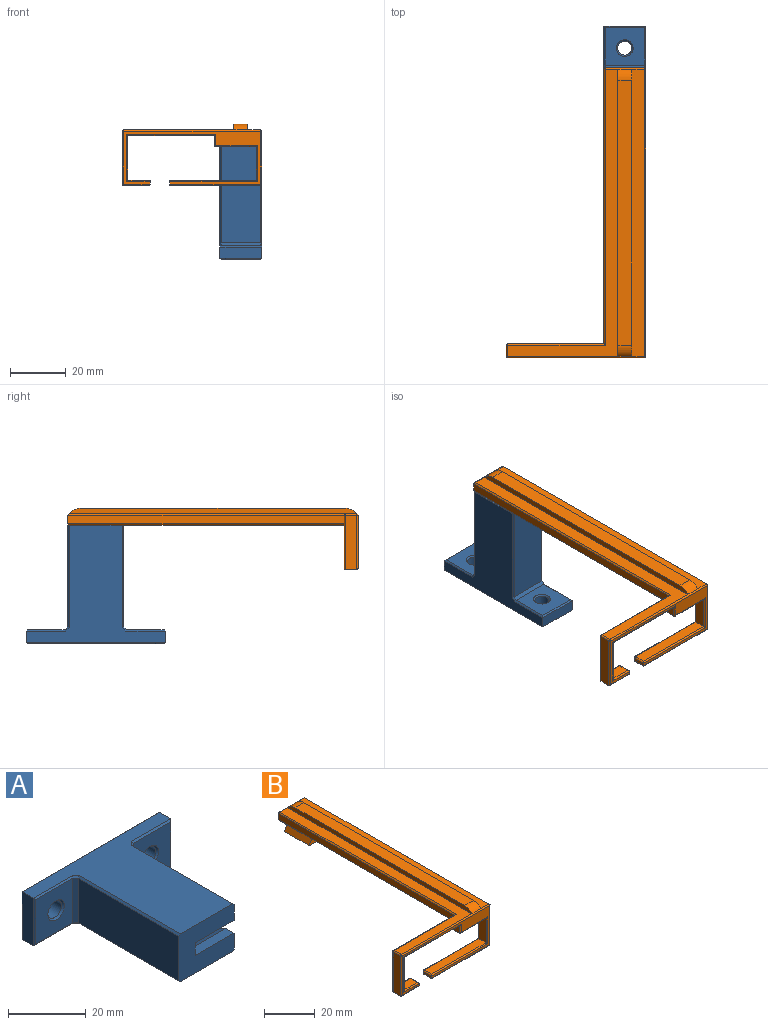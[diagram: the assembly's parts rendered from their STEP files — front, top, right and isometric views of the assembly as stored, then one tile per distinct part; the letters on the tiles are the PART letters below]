
ASSEMBLY  parts=2 mates=1
PART A: 42 faces, bbox 50x42.5x15 mm
  f0: plane 20x15mm, normal (0,-1,0), area 243.5mm2, adj f2,f4,f10,f11,f14,f18,f21,f26
  f1: plane 14x13.5mm, normal (0,-1,0), area 160.7mm2, adj f12,f23,f24,f25,f31
  f2: plane 50x42mm, normal (0,0,1), area 923.7mm2, adj f0,f3,f7,f14,f15,f16,f21,f22
  f3: plane 15x4mm, normal (-1,0,0), area 60mm2, adj f2,f4,f17,f35
  f4: plane 50x42mm, normal (0,0,-1), area 923.7mm2, adj f0,f3,f7,f18,f19,f20,f25,f26
  f5: cylinder r=2.5mm len=5mm, axis (0,1,0), area 62.8mm2, adj f29,f30
  f6: cylinder r=2.5mm len=5mm, axis (0,1,0), area 62.8mm2, adj f28,f31
  f7: plane 15x4mm, normal (1,0,0), area 60mm2, adj f2,f4,f24,f32
  f8: plane 14x13.5mm, normal (0,-1,0), area 160.7mm2, adj f13,f16,f17,f19,f30
  f9: plane 49x14mm, normal (0,1,0), area 629.5mm2, adj f28,f29,f32,f33,f34,f35
  f10: plane 36.5x14mm, normal (-1,0,0), area 511mm2, adj f0,f13,f14,f18
  f11: plane 36.5x14mm, normal (1,0,0), area 474.4mm2, adj f0,f12,f21,f26,f36,f37,f38,f39
  f12: plane 14x1mm, normal (0.71,-0.71,0), area 19.8mm2, adj f1,f11,f22,f27
  f13: plane 14x1mm, normal (-0.71,-0.71,0), area 19.8mm2, adj f8,f10,f15,f20
  f14: plane 36.71x0.5mm, normal (-0.71,0,0.71), area 25.9mm2, adj f0,f2,f10,f15
  f15: plane 1.5x1.5mm, normal (-0.5,-0.5,0.71), area 1.1mm2, adj f2,f13,f14,f16
  f16: plane 14.21x0.5mm, normal (0,-0.71,0.71), area 9.8mm2, adj f2,f8,f15,f17
  f17: plane 15x0.5mm, normal (-0.71,-0.71,0), area 10.3mm2, adj f3,f8,f16,f19
  f18: plane 36.71x0.5mm, normal (-0.71,0,-0.71), area 25.9mm2, adj f0,f4,f10,f20
  f19: plane 14.21x0.5mm, normal (0,-0.71,-0.71), area 9.8mm2, adj f4,f8,f17,f20
  f20: plane 1.5x1.5mm, normal (-0.5,-0.5,-0.71), area 1.1mm2, adj f4,f13,f18,f19
  f21: plane 36.71x0.5mm, normal (0.71,0,0.71), area 25.9mm2, adj f0,f2,f11,f22
  f22: plane 1.5x1.5mm, normal (0.5,-0.5,0.71), area 1.1mm2, adj f2,f12,f21,f23
  f23: plane 14.21x0.5mm, normal (0,-0.71,0.71), area 9.8mm2, adj f1,f2,f22,f24
  f24: plane 15x0.5mm, normal (0.71,-0.71,0), area 10.3mm2, adj f1,f7,f23,f25
  f25: plane 14.21x0.5mm, normal (0,-0.71,-0.71), area 9.8mm2, adj f1,f4,f24,f27
  f26: plane 36.71x0.5mm, normal (0.71,0,-0.71), area 25.9mm2, adj f0,f4,f11,f27
  f27: plane 1.5x1.5mm, normal (0.5,-0.5,-0.71), area 1.1mm2, adj f4,f12,f25,f26
  f28: cone r=3mm half-angle=45deg, axis (0,1,0), area 12.2mm2, adj f6,f9
  f29: cone r=3mm half-angle=45deg, axis (0,1,0), area 12.2mm2, adj f5,f9
  f30: cone r=2.5mm half-angle=45deg, axis (0,-1,0), area 12.2mm2, adj f5,f8
  f31: cone r=2.5mm half-angle=45deg, axis (0,-1,0), area 12.2mm2, adj f1,f6
  f32: plane 15x0.5mm, normal (0.71,0.71,0), area 10.3mm2, adj f7,f9,f33,f34
  f33: plane 50x0.5mm, normal (0,0.71,0.71), area 35mm2, adj f2,f9,f32,f35
  f34: plane 50x0.5mm, normal (0,0.71,-0.71), area 35mm2, adj f4,f9,f32,f35
  f35: plane 15x0.5mm, normal (-0.71,0.71,0), area 10.3mm2, adj f3,f9,f33,f34
  f36: plane 14x3mm, normal (0,0,1), area 42mm2, adj f0,f11,f37,f41
  f37: plane 14x4.1mm, normal (0,0.44,0.9), area 63.9mm2, adj f11,f36,f38,f41
  f38: plane 14x8mm, normal (0,-1,0), area 112mm2, adj f11,f37,f39,f41
  f39: plane 14x4.1mm, normal (0,0.44,-0.9), area 63.9mm2, adj f11,f38,f40,f41
  f40: plane 14x3mm, normal (0,0,-1), area 42mm2, adj f0,f11,f39,f41
  f41: plane 8x7.1mm, normal (1,0,0), area 36.6mm2, adj f0,f36,f37,f38,f39,f40
PART B: 74 faces, bbox 50x104x22 mm
  f0: plane 103x4.5mm, normal (0,0,1), area 463.5mm2, adj f28,f67,f68,f70
  f1: plane 9.5x4.5mm, normal (0,0,-1), area 42.7mm2, adj f2,f16,f55,f56,f60
  f2: plane 49x19.5mm, normal (0,1,0), area 137.9mm2, adj f1,f12,f14,f26,f32,f35,f36,f39
  f3: plane 30.5x4mm, normal (0,0,1), area 122mm2, adj f19,f37,f40,f41
  f4: plane 13.9x4.1mm, normal (-0.9,0,0.44), area 63.4mm2, adj f5,f8,f9,f10
  f5: plane 13.9x7.8mm, normal (0,0,-1), area 108.4mm2, adj f4,f6,f9,f10
  f6: plane 13.9x4.1mm, normal (0.9,0,0.44), area 63.4mm2, adj f5,f7,f9,f10
  f7: plane 13.9x3mm, normal (1,0,0), area 41.7mm2, adj f6,f9,f10,f14
  f8: plane 13.9x3mm, normal (-1,0,0), area 41.7mm2, adj f4,f9,f10,f14
  f9: plane 7.8x7.1mm, normal (0,-1,0), area 35.2mm2, adj f4,f5,f6,f7,f8,f14
  f10: plane 15x10.6mm, normal (0,1,0), area 87.4mm2, adj f4,f5,f6,f7,f8,f11,f12,f14
  f11: plane 103.5x19mm, normal (1,0,0), area 374.5mm2, adj f10,f27,f28,f49,f58,f65
  f12: plane 99x3mm, normal (-1,0,0), area 297mm2, adj f2,f10,f26,f29
  f13: plane 103x39.5mm, normal (0,0,1), area 603.5mm2, adj f29,f57,f64,f67,f68,f69
  f14: plane 99x14mm, normal (0,0,-1), area 1333.2mm2, adj f2,f7,f8,f9,f10,f26,f27
  f15: plane 32x4mm, normal (0,0,-1), area 128mm2, adj f50,f54,f58,f59
  f16: plane 19.5x4mm, normal (-1,0,0), area 78mm2, adj f1,f56,f63,f64
  f17: plane 49x19mm, normal (0,-1,0), area 185mm2, adj f24,f25,f30,f31,f33,f34,f37,f38
  f18: plane 15x4mm, normal (0,0,-1), area 60mm2, adj f19,f23,f30,f32
  f19: plane 12x4mm, normal (-1,0,0), area 48mm2, adj f3,f18,f33,f36
  f20: plane 7.5x4mm, normal (0,0,1), area 30mm2, adj f21,f42,f45,f46
  f21: plane 16x4mm, normal (1,0,0), area 64mm2, adj f20,f22,f38,f43
  f22: plane 31x4mm, normal (0,0,-1), area 124mm2, adj f21,f23,f34,f39
  f23: plane 4x4mm, normal (-1,0,0), area 16mm2, adj f18,f22,f31,f35
  f24: plane 4.5x1mm, normal (1,0,0), area 4.5mm2, adj f17,f45,f52,f55
  f25: plane 4.5x1mm, normal (-1,0,0), area 4.5mm2, adj f17,f41,f47,f54
  f26: plane 99x0.5mm, normal (-0.71,0,-0.71), area 70mm2, adj f2,f10,f12,f14
  f27: plane 99.5x0.5mm, normal (0.71,0,-0.71), area 70.1mm2, adj f10,f11,f14,f49
  f28: plane 103.93x0.5mm, normal (0.71,0,0.71), area 73.3mm2, adj f0,f11,f65,f67,f68
  f29: plane 99.5x0.5mm, normal (-0.71,0,0.71), area 70mm2, adj f12,f13,f57,f68
  f30: cylinder r=0.5mm len=15.5mm, axis (1,0,0), area 11.8mm2, adj f17,f18,f31,f33
  f31: cylinder r=0.5mm len=4.5mm, axis (0,0,-1), area 3.1mm2, adj f17,f23,f30,f34
  f32: cylinder r=0.5mm len=15.5mm, axis (1,0,0), area 11.8mm2, adj f2,f18,f35,f36
  f33: cylinder r=0.5mm len=13mm, axis (0,0,-1), area 9.7mm2, adj f17,f19,f30,f37
  f34: cylinder r=0.5mm len=32mm, axis (1,0,0), area 24.6mm2, adj f17,f22,f31,f38
  f35: cylinder r=0.5mm len=4.5mm, axis (0,0,-1), area 3.1mm2, adj f2,f23,f32,f39
  f36: cylinder r=0.5mm len=13mm, axis (0,0,-1), area 9.7mm2, adj f2,f19,f32,f40
  f37: cylinder r=0.5mm len=31.5mm, axis (-1,0,0), area 24.3mm2, adj f3,f17,f33,f41
  f38: cylinder r=0.5mm len=17mm, axis (0,0,1), area 12.9mm2, adj f17,f21,f34,f42
  f39: cylinder r=0.5mm len=32mm, axis (1,0,0), area 24.6mm2, adj f2,f22,f35,f43
  f40: cylinder r=0.5mm len=31mm, axis (-1,0,0), area 24.1mm2, adj f2,f3,f36,f44
  f41: cylinder r=0.5mm len=4.5mm, axis (0,1,0), area 3.4mm2, adj f3,f25,f37,f44
  f42: cylinder r=0.5mm len=8.5mm, axis (-1,0,0), area 6.3mm2, adj f17,f20,f38,f45
  f43: cylinder r=0.5mm len=17mm, axis (0,0,1), area 12.9mm2, adj f2,f21,f39,f46
  f44: sphere r=0.5mm, area 0.4mm2, adj f40,f41,f47
  f45: cylinder r=0.5mm len=4.5mm, axis (0,-1,0), area 3.4mm2, adj f20,f24,f42,f48
  f46: cylinder r=0.5mm len=8mm, axis (-1,0,0), area 6mm2, adj f2,f20,f43,f48
  f47: cylinder r=0.5mm len=1mm, axis (0,0,-1), area 0.8mm2, adj f2,f25,f44,f51
  f48: sphere r=0.5mm, area 0.4mm2, adj f45,f46,f52
  f49: cylinder r=0.5mm len=16mm, axis (0,0,1), area 12.4mm2, adj f2,f11,f27,f53
  f50: cylinder r=0.5mm len=32mm, axis (1,0,0), area 25.1mm2, adj f2,f15,f51,f53
  f51: sphere r=0.5mm, area 0.4mm2, adj f47,f50,f54
  f52: cylinder r=0.5mm len=1.5mm, axis (0,0,1), area 1mm2, adj f2,f24,f48,f55
  f53: sphere r=0.5mm, area 0.4mm2, adj f49,f50,f58
  f54: cylinder r=0.5mm len=4.5mm, axis (0,1,0), area 3.4mm2, adj f15,f25,f51,f59
  f55: cylinder r=0.5mm len=5mm, axis (0,-1,0), area 3.6mm2, adj f1,f24,f52,f60
  f56: cylinder r=0.5mm len=19.5mm, axis (0,0,-1), area 15.3mm2, adj f1,f2,f16,f61
  f57: cylinder r=0.5mm len=35mm, axis (1,0,0), area 27.3mm2, adj f2,f13,f29,f61
  f58: cylinder r=0.5mm len=4mm, axis (0,-1,0), area 3.1mm2, adj f11,f15,f53,f62
  f59: cylinder r=0.5mm len=32.5mm, axis (-1,0,0), area 25.4mm2, adj f15,f17,f54,f62
  f60: cylinder r=0.5mm len=10mm, axis (-1,0,0), area 7.6mm2, adj f1,f17,f55,f63
  f61: sphere r=0.5mm, area 0.4mm2, adj f56,f57,f64
  f62: sphere r=0.5mm, area 0.4mm2, adj f58,f59,f65
  f63: cylinder r=0.5mm len=19.5mm, axis (0,0,1), area 15.2mm2, adj f16,f17,f60,f66
  f64: cylinder r=0.5mm len=4mm, axis (0,-1,0), area 3.1mm2, adj f13,f16,f61,f66
  f65: cylinder r=0.5mm len=19.25mm, axis (0,0,-1), area 15mm2, adj f11,f17,f28,f62,f67
  f66: sphere r=0.5mm, area 0.4mm2, adj f63,f64,f67
  f67: cylinder r=0.5mm len=49.25mm, axis (-1,0,0), area 38.6mm2, adj f0,f13,f17,f28,f65,f66,f72
  f68: cylinder r=0.5mm len=15mm, axis (1,0,0), area 11.3mm2, adj f0,f10,f13,f28,f29,f73
  f69: plane 103x2mm, normal (-1,0,0), area 201.2mm2, adj f13,f71,f72,f73
  f70: plane 103x2mm, normal (1,0,0), area 201.2mm2, adj f0,f71,f72,f73
  f71: plane 95x5mm, normal (0,0,1), area 475mm2, adj f69,f70,f72,f73
  f72: cylinder r=5mm len=5mm, axis (-1,0,0), area 23.2mm2, adj f67,f69,f70,f71
  f73: cylinder r=5mm len=5mm, axis (1,0,0), area 23.2mm2, adj f68,f69,f70,f71
PLACE A rot(axis=(-0.58,-0.58,0.58),120deg) t=(104.43,49.1,-21.63)mm
PLACE B t=(108.53,69.37,17.87)mm
MATE fastened A.f38 <-> B.f5  axis (0,0,1) through (108.93,62.42,13.77)mm
